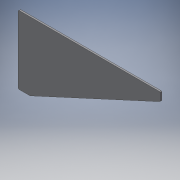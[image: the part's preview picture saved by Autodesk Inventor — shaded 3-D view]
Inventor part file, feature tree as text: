
AUTODESK INVENTOR PART (.ipt)
format: ipt  version: 2019 (Build 230136000, 136)  size: 181,248 bytes
history: native  units: in
note: dims shown in document units (in); Inventor stores cm internally (conversion verified against a paired STEP export)
features: reference x35, sketch x4, other x4, extrude x3, fillet x1, projected_geometry x1, helix x1
ambient origin geometry x8: Origin, YZ Plane, XZ Plane, XY Plane, X Axis, Y Axis, Z Axis, Center Point
bodies: Solid1 (feature_tree)
feature tree (49):
  extrude  "Extrusion1"  Depth=0.1575in TaperAngle=0.0deg
  fillet  "Fillet1"  Radius=0.0787in
  sketch  "Sketch2"  dims[d5=0.0079in d6=0.0079in]
  extrude  "Extrusion2"  Depth=0.0079in
  extrude  "Extrusion3"  Depth=0.0079in
  sketch  "Sketch1"  dims[d0=0.3937in d2=0.1575in d3=0.0in d4=0.0787in]
  reference  "Reference1"
  reference  "Reference2"
  reference  "Reference3"
  reference  "Reference4"
  sketch  "Sketch3"  dims[d7=0.0079in d8=0.0079in d9=0.126in]
  reference  "Reference5"
  reference  "Reference6"
  reference  "Reference7"
  reference  "Reference8"
  reference  "Reference9"
  reference  "Reference10"
  reference  "Reference11"
  reference  "Reference12"
  reference  "Reference13"
  reference  "Reference14"
  projected_geometry  "Projected Loop1"
  reference  "Reference15"
  reference  "Reference16"
  reference  "Reference17"
  reference  "Reference18"
  reference  "Reference19"
  reference  "Reference20"
  reference  "Reference21"
  reference  "Reference22"
  reference  "Reference23"
  reference  "Reference24"
  reference  "Reference25"
  reference  "Reference26"
  reference  "Reference27"
  reference  "Reference28"
  reference  "Reference29"
  reference  "Reference30"
  reference  "Reference31"
  reference  "Reference32"
  reference  "Reference33"
  reference  "Reference34"
  sketch  "Sketch4"  dims[d10=0.126in d11=0.1575in d12=0.0in d13=0.3937in d14=0.3937in d15=0.1969in d16=0.1969in d17=0.1575in d18=0.0in]
  reference  "Reference35"
  other  "<userpath>\Documents\CAD Files\Helix DLP\Helix DLP.iam"
  helix  "Helix DLP.iam"  [1 undecoded]
  other  "ProjectorMount 1:1"
  other  "30X30 - T-slot - Aluminium Profile_CPY_CPY:1"
  other  "Projector:1"
note: 1 required parameter value undecoded (feature->parameter linkage not recoverable at this tier; creation-order binding heuristic only, values carry confidence <= 0.55)
